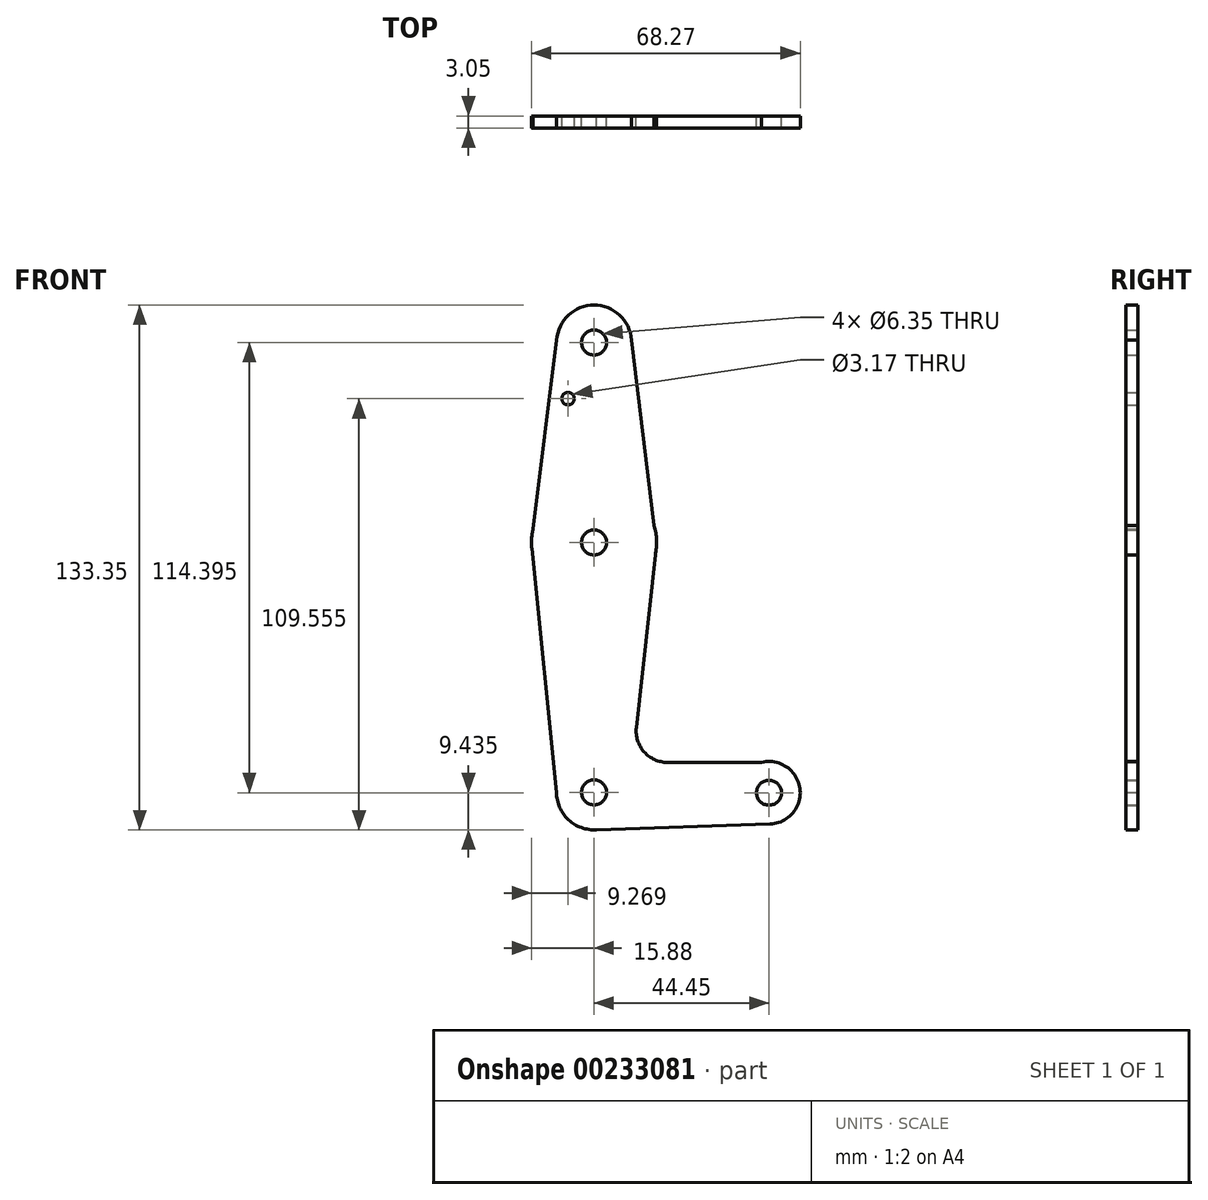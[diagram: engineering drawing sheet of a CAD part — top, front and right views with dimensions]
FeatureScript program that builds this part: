
annotation { "Feature Type Name" : "Feature", "Feature Type Description" : "" }
export const myFeature = defineFeature(function(context is Context, id is Id, definition is map)
    precondition{}
    {
        {
            var Q0;
            Q0=qCreatedBy(makeId("Front.planeOp"),FACE);
            var sketch = newSketch(context, id + "F0", { "sketchPlane" : qUnion([Q0])});
            skLineSegment(sketch, "E0", {"start": v(0, 0) * mm, "end": v(0, 50.8) * mm});
            skLineSegment(sketch, "E1", {"start": v(0, 0) * mm, "end": v(0, -63.5) * mm});
            skLineSegment(sketch, "E2", {"start": v(0, -63.5) * mm, "end": v(44.45, -63.6) * mm});
            skCircle(sketch, "E3", {"center": v(0, 0) * mm, "radius": 15.88 * mm});
            skCircle(sketch, "E4", {"center": v(0, -63.5) * mm, "radius": 9.53 * mm});
            skCircle(sketch, "E5", {"center": v(0, 50.8) * mm, "radius": 9.53 * mm});
            skCircle(sketch, "E6", {"center": v(44.45, -63.6) * mm, "radius": 7.94 * mm});
            skLineSegment(sketch, "E7", {"start": v(9.38, 52.47) * mm, "end": v(15.29, 4.29) * mm});
            skLineSegment(sketch, "E8", {"start": v(-9.5, 51.44) * mm, "end": v(-15.5, 3.47) * mm});
            skLineSegment(sketch, "E9", {"start": v(15.87, -0.26) * mm, "end": v(10.74, -47.07) * mm});
            skLineSegment(sketch, "E10", {"start": v(18.65, -55.88) * mm, "end": v(42.57, -55.88) * mm});
            skCircle(sketch, "E11", {"center": v(0, 50.8) * mm, "radius": 3.18 * mm});
            skCircle(sketch, "E12", {"center": v(-6.61, 36.53) * mm, "radius": 1.59 * mm});
            skCircle(sketch, "E13", {"center": v(0, 0) * mm, "radius": 3.17 * mm});
            skCircle(sketch, "E14", {"center": v(0, -63.5) * mm, "radius": 3.18 * mm});
            skCircle(sketch, "E15", {"center": v(44.45, -63.6) * mm, "radius": 3.18 * mm});
            skArc(sketch, "E16.filletArc", {"start": v(10.74, -47.07) * mm, "mid": v(12.73, -53.24) * mm, "end": v(18.65, -55.88) * mm});
            skLineSegment(sketch, "E17", {"start": v(-9.52, -63.5) * mm, "end": v(-15.8, -1.6) * mm});
            skLineSegment(sketch, "E18", {"start": v(0, -73.03) * mm, "end": v(44.72, -71.53) * mm});
            skSolve(sketch);
        }
        {
            var Q0;
            Q0 = qSketchRegion(id + "F0", true);
            var Q1;
            {var subQ0=sQuery(id+"F0.wireOp",EDGE,"E4");var subQ1=sQuery(id+"F0.wireOp",EDGE,"E1");var subQ2=makeQuery(id+"F0.imprint","INTERSECT",VERTEX,{"derivedFrom":[subQ1,subQ0]});Q1=makeQuery(id+"F0.imprint","IMPRINT",FACE,{"disambiguationData":[TD([[makeQuery(id+"F0.imprint","IMPRINT",EDGE,{"disambiguationData":[TD([[subQ2,-1.0]])],"derivedFrom":subQ1}),1.0]])]});}
            extrude(context, id + "F1", {"entities" : qUnion([Q0, Q1]), "depth" : 3.05 * mm});
        }
    });
